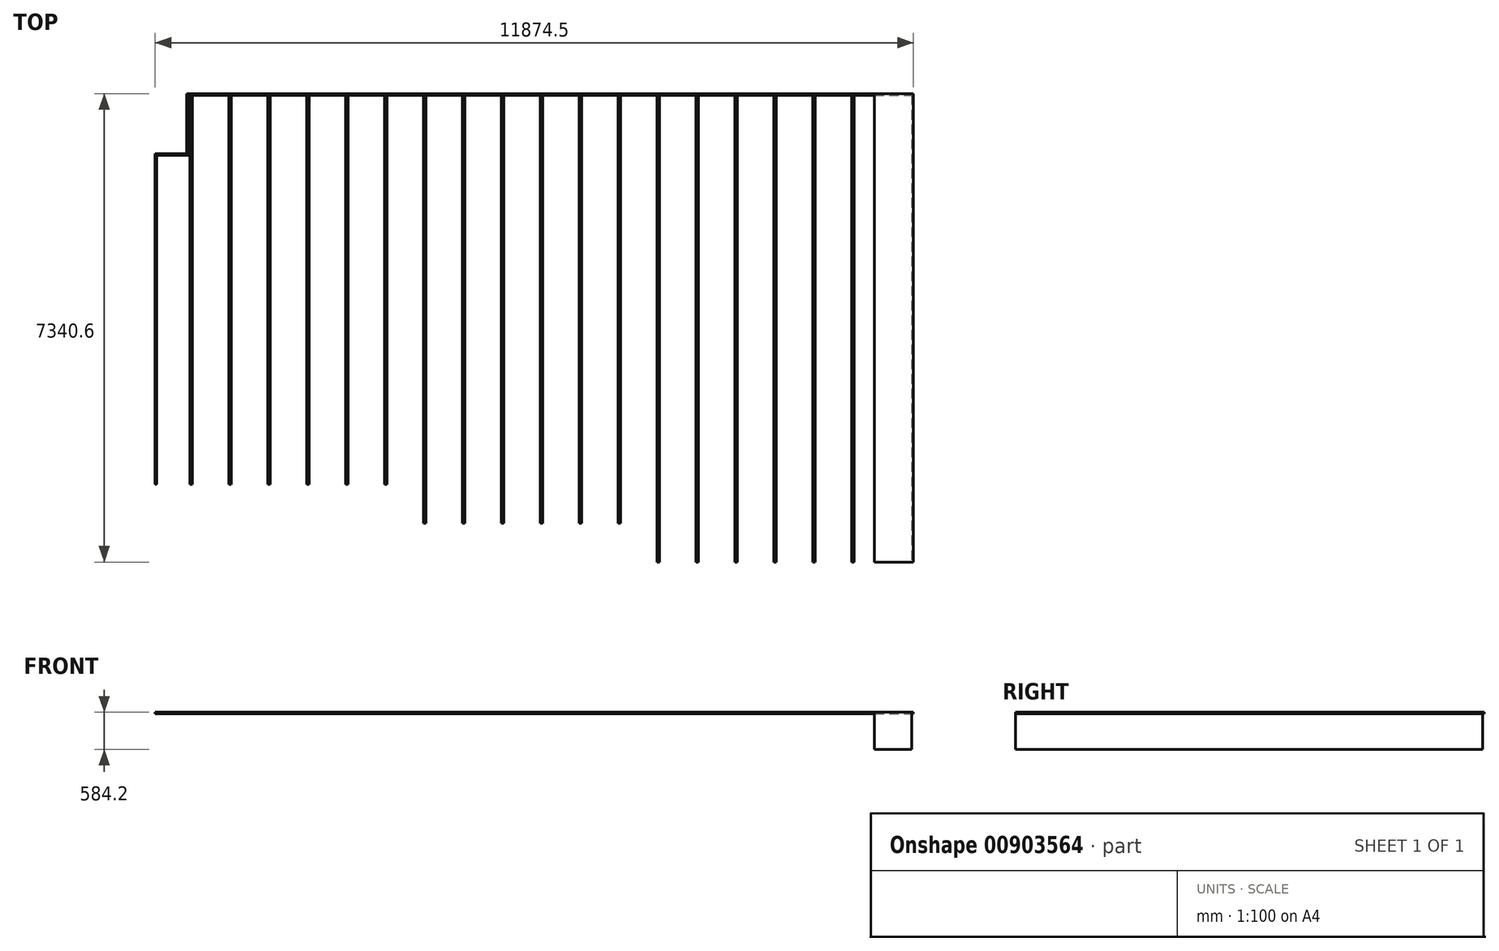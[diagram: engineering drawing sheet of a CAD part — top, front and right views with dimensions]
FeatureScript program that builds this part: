
annotation { "Feature Type Name" : "Feature", "Feature Type Description" : "" }
export const myFeature = defineFeature(function(context is Context, id is Id, definition is map)
    precondition{}
    {
        {
            var Q0;
            Q0=qCreatedBy(makeId("Top.planeOp"),FACE);
            var sketch = newSketch(context, id + "F0", { "sketchPlane" : qUnion([Q0])});
            skLineSegment(sketch, "E0.bottom", {"start": v(-7938.17, 1955.44) * mm, "end": v(2806.03, 1955.44) * mm});
            skLineSegment(sketch, "E0.right", {"start": v(2806.03, 1955.44) * mm, "end": v(2806.03, -5359.76) * mm});
            skLineSegment(sketch, "E1.top", {"start": v(-7938.17, -4140.56) * mm, "end": v(-4432.97, -4140.56) * mm});
            skLineSegment(sketch, "E2.top", {"start": v(-4432.97, -4750.16) * mm, "end": v(-927.77, -4750.16) * mm});
            skLineSegment(sketch, "E2.right", {"start": v(-927.77, -4750.16) * mm, "end": v(-927.77, -5359.76) * mm});
            skLineSegment(sketch, "E3.bottom", {"start": v(-927.77, -5359.76) * mm, "end": v(5322.66, -5359.76) * mm});
            skLineSegment(sketch, "E3.top", {"start": v(-927.77, -5359.76) * mm, "end": v(5322.66, -5359.76) * mm});
            skLineSegment(sketch, "E3.left", {"start": v(-927.77, -5359.76) * mm, "end": v(-927.77, -5359.76) * mm});
            skLineSegment(sketch, "E3.right", {"start": v(5322.66, -5359.76) * mm, "end": v(5322.66, -5359.76) * mm});
            skLineSegment(sketch, "E4", {"start": v(-4432.97, -4140.56) * mm, "end": v(-4432.97, -4750.16) * mm});
            skLineSegment(sketch, "E5", {"start": v(-7938.17, -4140.56) * mm, "end": v(-7938.17, 1955.44) * mm});
            skLineSegment(sketch, "E6.bottom", {"start": v(2806.03, 1955.44) * mm, "end": v(3390.23, 1955.44) * mm});
            skLineSegment(sketch, "E6.top", {"start": v(2806.03, -5359.76) * mm, "end": v(3390.23, -5359.76) * mm});
            skLineSegment(sketch, "E6.right", {"start": v(3390.23, 1955.44) * mm, "end": v(3390.23, -5359.76) * mm});
            skLineSegment(sketch, "E7", {"start": v(2488.53, 1955.44) * mm, "end": v(2488.53, -5359.76) * mm});
            skLineSegment(sketch, "E8", {"start": v(2450.43, 1955.44) * mm, "end": v(2450.43, -5359.76) * mm});
            skLineSegment(sketch, "E9", {"start": v(3060.03, 1955.44) * mm, "end": v(3060.03, -5359.76) * mm});
            skLineSegment(sketch, "E10", {"start": v(3098.13, 1955.44) * mm, "end": v(3098.13, -5359.76) * mm});
            skLineSegment(sketch, "E11.1.0.0", {"start": v(1878.93, 1955.44) * mm, "end": v(1878.93, -5359.76) * mm});
            skLineSegment(sketch, "E11.1.0.1", {"start": v(1840.83, 1955.44) * mm, "end": v(1840.83, -5359.76) * mm});
            skLineSegment(sketch, "E11.2.0.0", {"start": v(1269.33, 1955.44) * mm, "end": v(1269.33, -5359.76) * mm});
            skLineSegment(sketch, "E11.2.0.1", {"start": v(1231.23, 1955.44) * mm, "end": v(1231.23, -5359.76) * mm});
            skLineSegment(sketch, "E11.3.0.0", {"start": v(659.73, 1955.44) * mm, "end": v(659.73, -5359.76) * mm});
            skLineSegment(sketch, "E11.3.0.1", {"start": v(621.63, 1955.44) * mm, "end": v(621.63, -5359.76) * mm});
            skLineSegment(sketch, "E11.4.0.0", {"start": v(50.13, 1955.44) * mm, "end": v(50.13, -5359.76) * mm});
            skLineSegment(sketch, "E11.4.0.1", {"start": v(12.03, 1955.44) * mm, "end": v(12.03, -5359.76) * mm});
            skLineSegment(sketch, "E11.5.0.0", {"start": v(-559.47, 1955.44) * mm, "end": v(-559.47, -5359.76) * mm});
            skLineSegment(sketch, "E11.5.0.1", {"start": v(-597.57, 1955.44) * mm, "end": v(-597.57, -5359.76) * mm});
            skLineSegment(sketch, "E11.6.0.0", {"start": v(-1169.07, 1955.44) * mm, "end": v(-1169.07, -5359.76) * mm});
            skLineSegment(sketch, "E11.6.0.1", {"start": v(-1207.17, 1955.44) * mm, "end": v(-1207.17, -5359.76) * mm});
            skLineSegment(sketch, "E11.7.0.0", {"start": v(-1778.67, 1955.44) * mm, "end": v(-1778.67, -5359.76) * mm});
            skLineSegment(sketch, "E11.7.0.1", {"start": v(-1816.77, 1955.44) * mm, "end": v(-1816.77, -5359.76) * mm});
            skLineSegment(sketch, "E11.8.0.0", {"start": v(-2388.27, 1955.44) * mm, "end": v(-2388.27, -5359.76) * mm});
            skLineSegment(sketch, "E11.8.0.1", {"start": v(-2426.37, 1955.44) * mm, "end": v(-2426.37, -5359.76) * mm});
            skLineSegment(sketch, "E11.9.0.0", {"start": v(-2997.87, 1955.44) * mm, "end": v(-2997.87, -5359.76) * mm});
            skLineSegment(sketch, "E11.9.0.1", {"start": v(-3035.97, 1955.44) * mm, "end": v(-3035.97, -5359.76) * mm});
            skLineSegment(sketch, "E11.10.0.0", {"start": v(-3607.47, 1955.44) * mm, "end": v(-3607.47, -5359.76) * mm});
            skLineSegment(sketch, "E11.10.0.1", {"start": v(-3645.57, 1955.44) * mm, "end": v(-3645.57, -5359.76) * mm});
            skLineSegment(sketch, "E11.11.0.0", {"start": v(-4217.07, 1955.44) * mm, "end": v(-4217.07, -5359.76) * mm});
            skLineSegment(sketch, "E11.11.0.1", {"start": v(-4255.17, 1955.44) * mm, "end": v(-4255.17, -5359.76) * mm});
            skLineSegment(sketch, "E11.12.0.0", {"start": v(-4826.67, 1955.44) * mm, "end": v(-4826.67, -5359.76) * mm});
            skLineSegment(sketch, "E11.12.0.1", {"start": v(-4864.77, 1955.44) * mm, "end": v(-4864.77, -5359.76) * mm});
            skLineSegment(sketch, "E11.13.0.0", {"start": v(-5436.27, 1955.44) * mm, "end": v(-5436.27, -5359.76) * mm});
            skLineSegment(sketch, "E11.13.0.1", {"start": v(-5474.37, 1955.44) * mm, "end": v(-5474.37, -5359.76) * mm});
            skLineSegment(sketch, "E11.14.0.0", {"start": v(-6045.87, 1955.44) * mm, "end": v(-6045.87, -5359.76) * mm});
            skLineSegment(sketch, "E11.14.0.1", {"start": v(-6083.97, 1955.44) * mm, "end": v(-6083.97, -5359.76) * mm});
            skLineSegment(sketch, "E11.15.0.0", {"start": v(-6655.47, 1955.44) * mm, "end": v(-6655.47, -5359.76) * mm});
            skLineSegment(sketch, "E11.15.0.1", {"start": v(-6693.57, 1955.44) * mm, "end": v(-6693.57, -5359.76) * mm});
            skLineSegment(sketch, "E11.16.0.0", {"start": v(-7265.07, 1955.44) * mm, "end": v(-7265.07, -5359.76) * mm});
            skLineSegment(sketch, "E11.16.0.1", {"start": v(-7303.17, 1955.44) * mm, "end": v(-7303.17, -5359.76) * mm});
            skLineSegment(sketch, "E11.17.0.0", {"start": v(-7874.67, 1955.44) * mm, "end": v(-7874.67, -5359.76) * mm});
            skLineSegment(sketch, "E11.17.0.1", {"start": v(-7912.77, 1955.44) * mm, "end": v(-7912.77, -5359.76) * mm});
            skLineSegment(sketch, "E11.direction1", {"start": v(2450.43, -5359.76) * mm, "end": v(1840.83, -5359.76) * mm, "construction": true});
            skLineSegment(sketch, "E12.bottom", {"start": v(-7938.17, -4140.56) * mm, "end": v(-8433.47, -4140.56) * mm});
            skLineSegment(sketch, "E12.top", {"start": v(-7938.17, 1015.64) * mm, "end": v(-8433.47, 1015.64) * mm});
            skLineSegment(sketch, "E12.left", {"start": v(-7938.17, -4140.56) * mm, "end": v(-7938.17, 1015.64) * mm});
            skLineSegment(sketch, "E12.right", {"start": v(-8433.47, -4140.56) * mm, "end": v(-8433.47, 1015.64) * mm});
            skLineSegment(sketch, "E13.bottom", {"start": v(-8433.47, 1015.64) * mm, "end": v(-8458.87, 1015.64) * mm});
            skLineSegment(sketch, "E13.top", {"start": v(-8433.47, -4140.56) * mm, "end": v(-8458.87, -4140.56) * mm});
            skLineSegment(sketch, "E13.left", {"start": v(-8433.47, 1015.64) * mm, "end": v(-8433.47, -4140.56) * mm});
            skLineSegment(sketch, "E13.right", {"start": v(-8458.87, 1015.64) * mm, "end": v(-8458.87, -4140.56) * mm});
            skLineSegment(sketch, "E14.bottom", {"start": v(-7938.17, 1015.64) * mm, "end": v(-8458.87, 1015.64) * mm});
            skLineSegment(sketch, "E14.top", {"start": v(-7938.17, 1041.04) * mm, "end": v(-8458.87, 1041.04) * mm});
            skLineSegment(sketch, "E14.left", {"start": v(-7938.17, 1015.64) * mm, "end": v(-7938.17, 1041.04) * mm});
            skLineSegment(sketch, "E14.right", {"start": v(-8458.87, 1015.64) * mm, "end": v(-8458.87, 1041.04) * mm});
            skLineSegment(sketch, "E15.bottom", {"start": v(-7938.17, 1041.04) * mm, "end": v(-7963.57, 1041.04) * mm});
            skLineSegment(sketch, "E15.top", {"start": v(-7938.17, 1955.44) * mm, "end": v(-7963.57, 1955.44) * mm});
            skLineSegment(sketch, "E15.left", {"start": v(-7938.17, 1041.04) * mm, "end": v(-7938.17, 1955.44) * mm});
            skLineSegment(sketch, "E15.right", {"start": v(-7963.57, 1041.04) * mm, "end": v(-7963.57, 1955.44) * mm});
            skLineSegment(sketch, "E16.bottom", {"start": v(-7963.57, 1955.44) * mm, "end": v(3390.23, 1955.44) * mm});
            skLineSegment(sketch, "E16.top", {"start": v(-7963.57, 1980.84) * mm, "end": v(3390.23, 1980.84) * mm});
            skLineSegment(sketch, "E16.left", {"start": v(-7963.57, 1955.44) * mm, "end": v(-7963.57, 1980.84) * mm});
            skLineSegment(sketch, "E16.right", {"start": v(3390.23, 1955.44) * mm, "end": v(3390.23, 1980.84) * mm});
            skLineSegment(sketch, "E17.bottom", {"start": v(3390.23, -5359.76) * mm, "end": v(3415.63, -5359.76) * mm});
            skLineSegment(sketch, "E17.top", {"start": v(3390.23, 1980.84) * mm, "end": v(3415.63, 1980.84) * mm});
            skLineSegment(sketch, "E17.left", {"start": v(3390.23, -5359.76) * mm, "end": v(3390.23, 1980.84) * mm});
            skLineSegment(sketch, "E17.right", {"start": v(3415.63, -5359.76) * mm, "end": v(3415.63, 1980.84) * mm});
            skSolve(sketch);
        }
        {
            var Q0;
            {var subQ0=sQuery(id+"F0.wireOp",EDGE,"E6.right");Q0=makeQuery(id+"F0.imprint","IMPRINT",FACE,{"disambiguationData":[TD([[makeQuery(id+"F0.imprint","IMPRINT",EDGE,{"derivedFrom":subQ0}),1.0]])]});}
            var Q1;
            {var subQ40=sQuery(id+"F0.wireOp",EDGE,"E15.top");Q1=makeQuery(id+"F0.imprint","IMPRINT",FACE,{"disambiguationData":[TD([[makeQuery(id+"F0.imprint","IMPRINT",EDGE,{"derivedFrom":subQ40}),-1.0]])]});}
            var Q2;
            {var subQ3=sQuery(id+"F0.wireOp",EDGE,"E15.top");Q2=makeQuery(id+"F0.imprint","IMPRINT",FACE,{"disambiguationData":[TD([[makeQuery(id+"F0.imprint","IMPRINT",EDGE,{"derivedFrom":subQ3}),1.0]])]});}
            var Q3;
            {var subQ3=sQuery(id+"F0.wireOp",EDGE,"E12.top");Q3=makeQuery(id+"F0.imprint","IMPRINT",FACE,{"disambiguationData":[TD([[makeQuery(id+"F0.imprint","IMPRINT",EDGE,{"derivedFrom":subQ3}),-1.0]])]});}
            var Q4;
            Q4=makeQuery(id+"F0.imprint","IMPRINT",FACE,{"disambiguationData":[TD([[makeQuery(id+"F0.imprint","IMPRINT",EDGE,{"derivedFrom":sQuery(id+"F0.wireOp",EDGE,"E12.right")}),1.0]])]});
            extrude(context, id + "F1", {"entities" : qUnion([Q0, Q1, Q2, Q3, Q4]), "oppositeDirection" : true, "depth" : 25.4 * mm, "offsetDistance" : 25.4 * mm});
        }
        {
            var Q0;
            {var subQ0=sQuery(id+"F0.wireOp",EDGE,"E11.16.0.0");var subQ1=sQuery(id+"F0.wireOp",EDGE,"E0.bottom");var subQ2=makeQuery(id+"F0.imprint","INTERSECT",VERTEX,{"derivedFrom":[subQ1,subQ0]});Q0=makeQuery(id+"F0.imprint","IMPRINT",FACE,{"disambiguationData":[TD([[makeQuery(id+"F0.imprint","IMPRINT",EDGE,{"disambiguationData":[TD([[subQ2,1.0]])],"derivedFrom":subQ1}),-1.0]])]});}
            var Q1;
            {var subQ0=sQuery(id+"F0.wireOp",EDGE,"E11.15.0.0");var subQ1=sQuery(id+"F0.wireOp",EDGE,"E0.bottom");var subQ2=makeQuery(id+"F0.imprint","INTERSECT",VERTEX,{"derivedFrom":[subQ1,subQ0]});Q1=makeQuery(id+"F0.imprint","IMPRINT",FACE,{"disambiguationData":[TD([[makeQuery(id+"F0.imprint","IMPRINT",EDGE,{"disambiguationData":[TD([[subQ2,1.0]])],"derivedFrom":subQ1}),-1.0]])]});}
            var Q2;
            {var subQ0=sQuery(id+"F0.wireOp",EDGE,"E11.14.0.0");var subQ1=sQuery(id+"F0.wireOp",EDGE,"E0.bottom");var subQ2=makeQuery(id+"F0.imprint","INTERSECT",VERTEX,{"derivedFrom":[subQ1,subQ0]});Q2=makeQuery(id+"F0.imprint","IMPRINT",FACE,{"disambiguationData":[TD([[makeQuery(id+"F0.imprint","IMPRINT",EDGE,{"disambiguationData":[TD([[subQ2,1.0]])],"derivedFrom":subQ1}),-1.0]])]});}
            var Q3;
            {var subQ0=sQuery(id+"F0.wireOp",EDGE,"E11.13.0.0");var subQ1=sQuery(id+"F0.wireOp",EDGE,"E0.bottom");var subQ2=makeQuery(id+"F0.imprint","INTERSECT",VERTEX,{"derivedFrom":[subQ1,subQ0]});Q3=makeQuery(id+"F0.imprint","IMPRINT",FACE,{"disambiguationData":[TD([[makeQuery(id+"F0.imprint","IMPRINT",EDGE,{"disambiguationData":[TD([[subQ2,1.0]])],"derivedFrom":subQ1}),-1.0]])]});}
            var Q4;
            {var subQ0=sQuery(id+"F0.wireOp",EDGE,"E11.12.0.0");var subQ1=sQuery(id+"F0.wireOp",EDGE,"E0.bottom");var subQ2=makeQuery(id+"F0.imprint","INTERSECT",VERTEX,{"derivedFrom":[subQ1,subQ0]});Q4=makeQuery(id+"F0.imprint","IMPRINT",FACE,{"disambiguationData":[TD([[makeQuery(id+"F0.imprint","IMPRINT",EDGE,{"disambiguationData":[TD([[subQ2,1.0]])],"derivedFrom":subQ1}),-1.0]])]});}
            var Q5;
            {var subQ0=sQuery(id+"F0.wireOp",EDGE,"E11.11.0.0");var subQ1=sQuery(id+"F0.wireOp",EDGE,"E0.bottom");var subQ2=makeQuery(id+"F0.imprint","INTERSECT",VERTEX,{"derivedFrom":[subQ1,subQ0]});Q5=makeQuery(id+"F0.imprint","IMPRINT",FACE,{"disambiguationData":[TD([[makeQuery(id+"F0.imprint","IMPRINT",EDGE,{"disambiguationData":[TD([[subQ2,1.0]])],"derivedFrom":subQ1}),-1.0]])]});}
            var Q6;
            {var subQ0=sQuery(id+"F0.wireOp",EDGE,"E11.10.0.0");var subQ1=sQuery(id+"F0.wireOp",EDGE,"E0.bottom");var subQ2=makeQuery(id+"F0.imprint","INTERSECT",VERTEX,{"derivedFrom":[subQ1,subQ0]});Q6=makeQuery(id+"F0.imprint","IMPRINT",FACE,{"disambiguationData":[TD([[makeQuery(id+"F0.imprint","IMPRINT",EDGE,{"disambiguationData":[TD([[subQ2,1.0]])],"derivedFrom":subQ1}),-1.0]])]});}
            var Q7;
            {var subQ0=sQuery(id+"F0.wireOp",EDGE,"E11.9.0.0");var subQ1=sQuery(id+"F0.wireOp",EDGE,"E0.bottom");var subQ2=makeQuery(id+"F0.imprint","INTERSECT",VERTEX,{"derivedFrom":[subQ1,subQ0]});Q7=makeQuery(id+"F0.imprint","IMPRINT",FACE,{"disambiguationData":[TD([[makeQuery(id+"F0.imprint","IMPRINT",EDGE,{"disambiguationData":[TD([[subQ2,1.0]])],"derivedFrom":subQ1}),-1.0]])]});}
            var Q8;
            {var subQ0=sQuery(id+"F0.wireOp",EDGE,"E11.8.0.0");var subQ1=sQuery(id+"F0.wireOp",EDGE,"E0.bottom");var subQ2=makeQuery(id+"F0.imprint","INTERSECT",VERTEX,{"derivedFrom":[subQ1,subQ0]});Q8=makeQuery(id+"F0.imprint","IMPRINT",FACE,{"disambiguationData":[TD([[makeQuery(id+"F0.imprint","IMPRINT",EDGE,{"disambiguationData":[TD([[subQ2,1.0]])],"derivedFrom":subQ1}),-1.0]])]});}
            var Q9;
            {var subQ0=sQuery(id+"F0.wireOp",EDGE,"E11.17.0.1");var subQ1=sQuery(id+"F0.wireOp",EDGE,"E0.bottom");var subQ2=makeQuery(id+"F0.imprint","INTERSECT",VERTEX,{"derivedFrom":[subQ1,subQ0]});Q9=makeQuery(id+"F0.imprint","IMPRINT",FACE,{"disambiguationData":[TD([[makeQuery(id+"F0.imprint","IMPRINT",EDGE,{"disambiguationData":[TD([[subQ2,-1.0]])],"derivedFrom":subQ1}),-1.0]])]});}
            var Q10;
            {var subQ0=sQuery(id+"F0.wireOp",EDGE,"E11.7.0.0");var subQ1=sQuery(id+"F0.wireOp",EDGE,"E0.bottom");var subQ2=makeQuery(id+"F0.imprint","INTERSECT",VERTEX,{"derivedFrom":[subQ1,subQ0]});Q10=makeQuery(id+"F0.imprint","IMPRINT",FACE,{"disambiguationData":[TD([[makeQuery(id+"F0.imprint","IMPRINT",EDGE,{"disambiguationData":[TD([[subQ2,1.0]])],"derivedFrom":subQ1}),-1.0]])]});}
            var Q11;
            {var subQ0=sQuery(id+"F0.wireOp",EDGE,"E11.6.0.0");var subQ1=sQuery(id+"F0.wireOp",EDGE,"E0.bottom");var subQ2=makeQuery(id+"F0.imprint","INTERSECT",VERTEX,{"derivedFrom":[subQ1,subQ0]});Q11=makeQuery(id+"F0.imprint","IMPRINT",FACE,{"disambiguationData":[TD([[makeQuery(id+"F0.imprint","IMPRINT",EDGE,{"disambiguationData":[TD([[subQ2,1.0]])],"derivedFrom":subQ1}),-1.0]])]});}
            var Q12;
            {var subQ0=sQuery(id+"F0.wireOp",EDGE,"E11.5.0.0");Q12=makeQuery(id+"F0.imprint","IMPRINT",FACE,{"disambiguationData":[TD([[makeQuery(id+"F0.imprint","IMPRINT",EDGE,{"derivedFrom":subQ0}),-1.0]])]});}
            var Q13;
            {var subQ0=sQuery(id+"F0.wireOp",EDGE,"E11.4.0.0");Q13=makeQuery(id+"F0.imprint","IMPRINT",FACE,{"disambiguationData":[TD([[makeQuery(id+"F0.imprint","IMPRINT",EDGE,{"derivedFrom":subQ0}),-1.0]])]});}
            var Q14;
            {var subQ0=sQuery(id+"F0.wireOp",EDGE,"E11.3.0.0");Q14=makeQuery(id+"F0.imprint","IMPRINT",FACE,{"disambiguationData":[TD([[makeQuery(id+"F0.imprint","IMPRINT",EDGE,{"derivedFrom":subQ0}),-1.0]])]});}
            var Q15;
            {var subQ0=sQuery(id+"F0.wireOp",EDGE,"E11.2.0.0");Q15=makeQuery(id+"F0.imprint","IMPRINT",FACE,{"disambiguationData":[TD([[makeQuery(id+"F0.imprint","IMPRINT",EDGE,{"derivedFrom":subQ0}),-1.0]])]});}
            var Q16;
            {var subQ0=sQuery(id+"F0.wireOp",EDGE,"E11.1.0.0");Q16=makeQuery(id+"F0.imprint","IMPRINT",FACE,{"disambiguationData":[TD([[makeQuery(id+"F0.imprint","IMPRINT",EDGE,{"derivedFrom":subQ0}),-1.0]])]});}
            var Q17;
            {var subQ0=sQuery(id+"F0.wireOp",EDGE,"E7");Q17=makeQuery(id+"F0.imprint","IMPRINT",FACE,{"disambiguationData":[TD([[makeQuery(id+"F0.imprint","IMPRINT",EDGE,{"derivedFrom":subQ0}),-1.0]])]});}
            var Q18;
            {var subQ0=sQuery(id+"F0.wireOp",EDGE,"E9");Q18=makeQuery(id+"F0.imprint","IMPRINT",FACE,{"disambiguationData":[TD([[makeQuery(id+"F0.imprint","IMPRINT",EDGE,{"derivedFrom":subQ0}),1.0]])]});}
            extrude(context, id + "F2", {"entities" : qUnion([Q0, Q1, Q2, Q3, Q4, Q5, Q6, Q7, Q8, Q9, Q10, Q11, Q12, Q13, Q14, Q15, Q16, Q17, Q18]), "operationType" : NewBodyOperationType.ADD, "oppositeDirection" : true, "depth" : 25.4 * mm, "offsetDistance" : 25.4 * mm});
        }
        {
            var Q0;
            {var subQ0=sQuery(id+"F0.wireOp",EDGE,"E6.right");Q0=makeQuery(id+"F0.imprint","IMPRINT",FACE,{"disambiguationData":[TD([[makeQuery(id+"F0.imprint","IMPRINT",EDGE,{"derivedFrom":subQ0}),-1.0]])]});}
            var Q1;
            {var subQ0=sQuery(id+"F0.wireOp",EDGE,"E0.right");Q1=makeQuery(id+"F0.imprint","IMPRINT",FACE,{"disambiguationData":[TD([[makeQuery(id+"F0.imprint","IMPRINT",EDGE,{"derivedFrom":subQ0}),1.0]])]});}
            var Q2;
            {var subQ0=sQuery(id+"F0.wireOp",EDGE,"E9");Q2=makeQuery(id+"F0.imprint","IMPRINT",FACE,{"disambiguationData":[TD([[makeQuery(id+"F0.imprint","IMPRINT",EDGE,{"derivedFrom":subQ0}),1.0]])]});}
            extrude(context, id + "F3", {"entities" : qUnion([Q0, Q1, Q2]), "operationType" : NewBodyOperationType.ADD, "oppositeDirection" : true, "depth" : 584.2 * mm, "offsetDistance" : 25.4 * mm});
        }
    });
